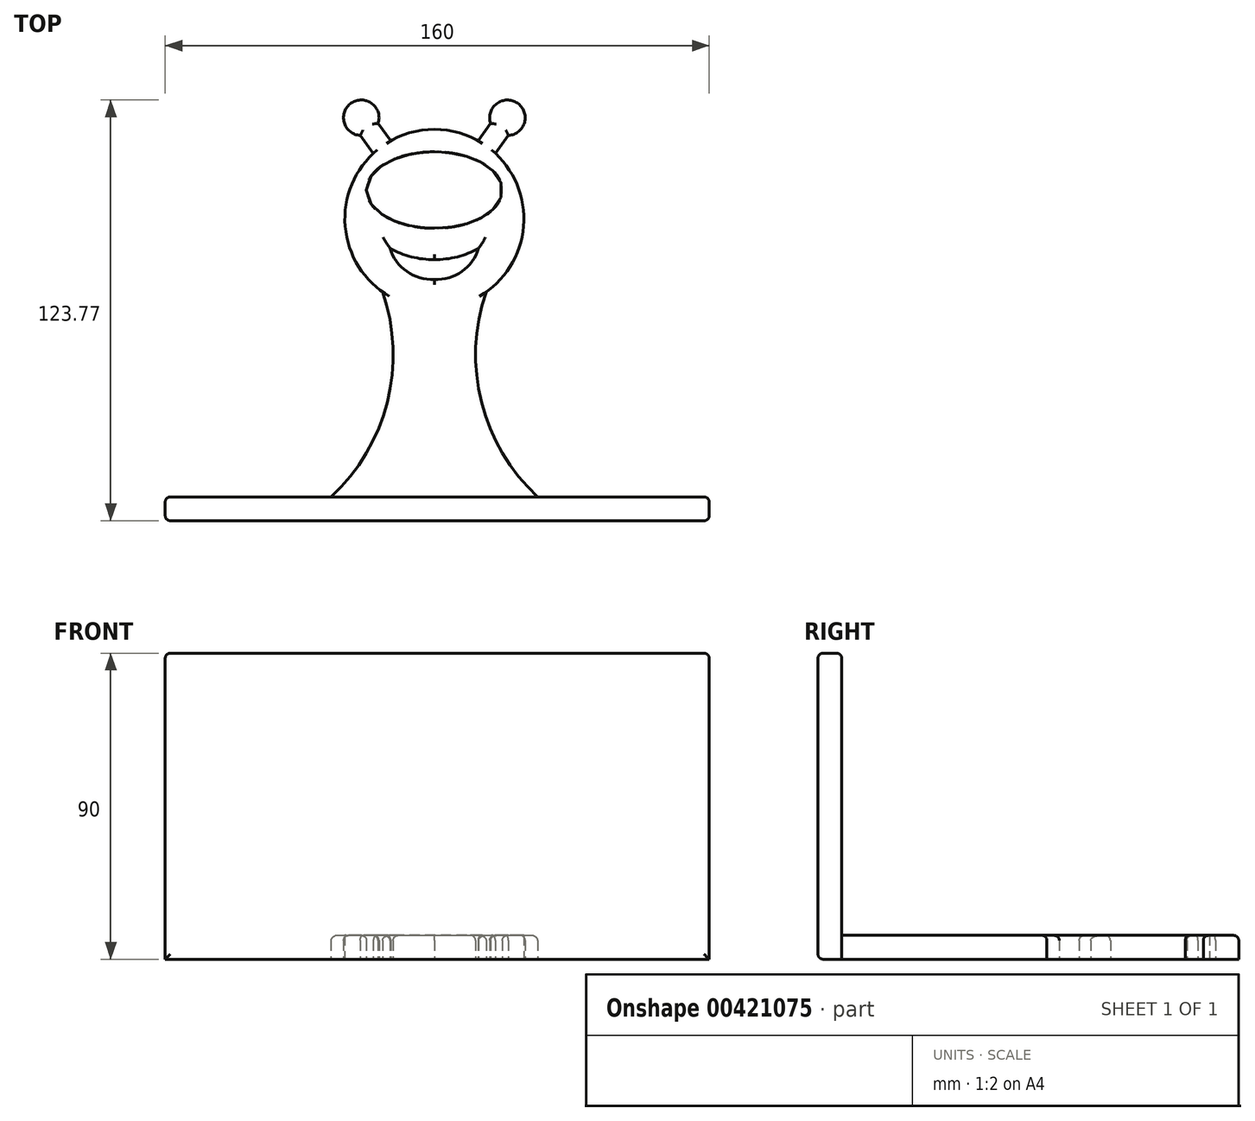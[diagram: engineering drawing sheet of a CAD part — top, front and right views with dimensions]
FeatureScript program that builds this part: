
annotation { "Feature Type Name" : "Feature", "Feature Type Description" : "" }
export const myFeature = defineFeature(function(context is Context, id is Id, definition is map)
    precondition{}
    {
        {
            var Q0;
            Q0=qCreatedBy(makeId("Top.planeOp"),FACE);
            var sketch = newSketch(context, id + "F0", { "sketchPlane" : qUnion([Q0])});
            skLineSegment(sketch, "E0", {"start": v(0, 25.53) * mm, "end": v(-30.48, 25.53) * mm});
            skArc(sketch, "E1", {"start": v(0, 25.53) * mm, "mid": v(-15.24, 73.33) * mm, "end": v(-30.48, 25.53) * mm});
            skArc(sketch, "E2", {"start": v(-45.92, -35.04) * mm, "mid": v(-29.13, -7.07) * mm, "end": v(-30.48, 25.53) * mm});
            skLineSegment(sketch, "E3", {"start": v(-45.92, -35.04) * mm, "end": v(-15.24, -35.04) * mm});
            skLineSegment(sketch, "E4", {"start": v(-15.24, 85.1) * mm, "end": v(-15.24, -44.22) * mm, "construction": true});
            skLineSegment(sketch, "E5.MirrorCS", {"start": v(-30.48, 25.53) * mm, "end": v(0, 25.53) * mm});
            skArc(sketch, "E6.MirrorCS", {"start": v(-30.48, 25.53) * mm, "mid": v(-15.24, 73.33) * mm, "end": v(0, 25.53) * mm});
            skArc(sketch, "E7.MirrorCS", {"start": v(15.44, -35.04) * mm, "mid": v(-1.35, -7.07) * mm, "end": v(0, 25.53) * mm});
            skLineSegment(sketch, "E8.MirrorCS", {"start": v(15.44, -35.04) * mm, "end": v(-15.24, -35.04) * mm});
            skLineSegment(sketch, "E9", {"start": v(-33.18, 66.27) * mm, "end": v(-37.04, 71.54) * mm});
            skLineSegment(sketch, "E10", {"start": v(-28.05, 70) * mm, "end": v(-31.78, 75.1) * mm});
            skArc(sketch, "E11", {"start": v(-31.78, 75.1) * mm, "mid": v(-39.66, 81.08) * mm, "end": v(-37.04, 71.54) * mm});
            skLineSegment(sketch, "E12.MirrorCS", {"start": v(-2.43, 70) * mm, "end": v(1.3, 75.1) * mm});
            skArc(sketch, "E13.MirrorCS", {"start": v(1.3, 75.1) * mm, "mid": v(9.18, 81.08) * mm, "end": v(6.56, 71.54) * mm});
            skLineSegment(sketch, "E14.MirrorCS", {"start": v(2.7, 66.27) * mm, "end": v(6.56, 71.54) * mm});
            skEllipse(sketch, "E15", {"center": v(-15.24, 55.48) * mm, "majorRadius": 20 * mm, "minorRadius": 11.25 * mm, "majorAxis": v(-1, 0)});
            skLineSegment(sketch, "E16", {"start": v(-50.04, 38.4) * mm, "end": v(18.05, 38.4) * mm, "construction": true});
            skArc(sketch, "E17", {"start": v(-28.27, 38.4) * mm, "mid": v(-23.35, 31.54) * mm, "end": v(-15.24, 29.2) * mm});
            skArc(sketch, "E18.MirrorCS", {"start": v(-2.21, 38.4) * mm, "mid": v(-7.13, 31.54) * mm, "end": v(-15.24, 29.2) * mm});
            skPoint(sketch, "E19", {"position": v(-51.66, 25.2) * mm});
            skArc(sketch, "E20", {"start": v(-28.27, 38.4) * mm, "mid": v(-21.98, 35.83) * mm, "end": v(-15.24, 35.05) * mm});
            skArc(sketch, "E21.MirrorCS", {"start": v(-2.21, 38.4) * mm, "mid": v(-8.5, 35.83) * mm, "end": v(-15.24, 35.05) * mm});
            skSolve(sketch);
        }
        {
            var Q0;
            Q0 = qSketchRegion(id + "F0", true);
            extrude(context, id + "F1", {"entities" : qUnion([Q0]), "depth" : 7 * mm, "offsetDistance" : 25 * mm});
        }
        {
            var Q0;
            Q0=makeQuery(id+"F1.opExtrude","SWEPT_FACE",FACE,{"disambiguationData":[OSD([sQuery(id+"F0.wireOp",EDGE,"E3"),sQuery(id+"F0.wireOp",EDGE,"E8.MirrorCS")])]});
            cPlane(context, id + "F2", {"entities" : qUnion([Q0]), "cplaneType" : CPlaneType.OFFSET, "offset" : 0.24 * mm, "oppositeDirection" : true, "width" : 150 * mm, "height" : 150 * mm});
        }
        {
            var Q0;
            Q0=qCreatedBy(id+"F2.planeOp",FACE);
            var sketch = newSketch(context, id + "F3", { "sketchPlane" : qUnion([Q0])});
            skLineSegment(sketch, "E22", {"start": v(-14.4, 9.68) * mm, "end": v(-14.4, -13.08) * mm, "construction": true});
            skLineSegment(sketch, "E23", {"start": v(-14.4, 0) * mm, "end": v(-94.4, 0) * mm});
            skLineSegment(sketch, "E24.MirrorCS", {"start": v(-14.4, 0) * mm, "end": v(65.6, 0) * mm});
            skLineSegment(sketch, "E25", {"start": v(-94.4, 0) * mm, "end": v(-94.4, 90) * mm});
            skLineSegment(sketch, "E26.MirrorCS", {"start": v(65.6, 0) * mm, "end": v(65.6, 90) * mm});
            skLineSegment(sketch, "E27", {"start": v(-94.4, 90) * mm, "end": v(65.6, 90) * mm});
            skSolve(sketch);
        }
        {
            var Q0;
            Q0 = qSketchRegion(id + "F3", true);
            extrude(context, id + "F4", {"entities" : qUnion([Q0]), "operationType" : NewBodyOperationType.ADD, "depth" : 7 * mm, "offsetDistance" : 25 * mm});
        }
        {
            var Q0;
            Q0=makeQuery(id+"F1.opExtrude","CAP_EDGE",EDGE,{"disambiguationData":[OSD([sQuery(id+"F0.wireOp",EDGE,"E13.MirrorCS")])],"isStart":false});
            var Q1;
            Q1=makeQuery(id+"F1.opExtrude","CAP_EDGE",EDGE,{"disambiguationData":[OSD([sQuery(id+"F0.wireOp",EDGE,"E12.MirrorCS")])],"isStart":false});
            var Q2;
            Q2=makeQuery(id+"F1.opExtrude","CAP_EDGE",EDGE,{"disambiguationData":[OSD([sQuery(id+"F0.wireOp",EDGE,"E14.MirrorCS")])],"isStart":false});
            var Q3;
            Q3=makeQuery(id+"F1.opExtrude","CAP_EDGE",EDGE,{"disambiguationData":[OSD([sQuery(id+"F0.wireOp",EDGE,"E11")])],"isStart":false});
            var Q4;
            Q4=makeQuery(id+"F1.opExtrude","CAP_EDGE",EDGE,{"disambiguationData":[OSD([sQuery(id+"F0.wireOp",EDGE,"E10")])],"isStart":false});
            var Q5;
            Q5=makeQuery(id+"F1.opExtrude","CAP_EDGE",EDGE,{"disambiguationData":[OSD([sQuery(id+"F0.wireOp",EDGE,"E9")])],"isStart":false});
            var Q6;
            {var subQ0=sQuery(id+"F0.wireOp",EDGE,"E6.MirrorCS");Q6=makeQuery(id+"F1.opExtrude","CAP_EDGE",EDGE,{"disambiguationData":[OSD([subQ0]),TDD([makeQuery(id+"F0.imprint","IMPRINT",EDGE,{"disambiguationData":[TD([[makeQuery(id+"F0.imprint","INTERSECT",VERTEX,{"derivedFrom":[subQ0,sQuery(id+"F0.wireOp",EDGE,"E10")]}),-1.0]])],"derivedFrom":subQ0})])],"isStart":false});}
            var Q7;
            {var subQ0=sQuery(id+"F0.wireOp",EDGE,"E6.MirrorCS");Q7=makeQuery(id+"F1.opExtrude","CAP_EDGE",EDGE,{"disambiguationData":[OSD([subQ0]),TDD([makeQuery(id+"F0.imprint","IMPRINT",EDGE,{"disambiguationData":[TD([[makeQuery(id+"F0.imprint","INTERSECT",VERTEX,{"derivedFrom":[subQ0,sQuery(id+"F0.wireOp",EDGE,"E9")]}),1.0]])],"derivedFrom":subQ0})])],"isStart":false});}
            var Q8;
            {var subQ0=sQuery(id+"F0.wireOp",EDGE,"E6.MirrorCS");Q8=makeQuery(id+"F1.opExtrude","CAP_EDGE",EDGE,{"disambiguationData":[OSD([subQ0]),TDD([makeQuery(id+"F0.imprint","IMPRINT",EDGE,{"disambiguationData":[TD([[makeQuery(id+"F0.imprint","INTERSECT",VERTEX,{"derivedFrom":[subQ0,sQuery(id+"F0.wireOp",EDGE,"E14.MirrorCS")]}),-1.0]])],"derivedFrom":subQ0})])],"isStart":false});}
            var Q9;
            Q9=makeQuery(id+"F1.opExtrude","CAP_EDGE",EDGE,{"disambiguationData":[OSD([sQuery(id+"F0.wireOp",EDGE,"E15")])],"isStart":false});
            var Q10;
            Q10=makeQuery(id+"F1.opExtrude","CAP_EDGE",EDGE,{"disambiguationData":[OSD([sQuery(id+"F0.wireOp",EDGE,"E20")])],"isStart":false});
            var Q11;
            Q11=makeQuery(id+"F1.opExtrude","CAP_EDGE",EDGE,{"disambiguationData":[OSD([sQuery(id+"F0.wireOp",EDGE,"E21.MirrorCS")])],"isStart":false});
            var Q12;
            Q12=makeQuery(id+"F1.opExtrude","CAP_EDGE",EDGE,{"disambiguationData":[OSD([sQuery(id+"F0.wireOp",EDGE,"E18.MirrorCS")])],"isStart":false});
            var Q13;
            Q13=makeQuery(id+"F1.opExtrude","CAP_EDGE",EDGE,{"disambiguationData":[OSD([sQuery(id+"F0.wireOp",EDGE,"E17")])],"isStart":false});
            var Q14;
            Q14=makeQuery(id+"F1.opExtrude","CAP_EDGE",EDGE,{"disambiguationData":[OSD([sQuery(id+"F0.wireOp",EDGE,"E7.MirrorCS")])],"isStart":false});
            var Q15;
            Q15=makeQuery(id+"F1.opExtrude","CAP_EDGE",EDGE,{"disambiguationData":[OSD([sQuery(id+"F0.wireOp",EDGE,"E2")])],"isStart":false});
            var Q16;
            Q16=makeQuery(id+"F4.opExtrude","CAP_EDGE",EDGE,{"disambiguationData":[OSD([sQuery(id+"F3.wireOp",EDGE,"E25")])],"isStart":true});
            var Q17;
            Q17=makeQuery(id+"F4.opExtrude","CAP_EDGE",EDGE,{"disambiguationData":[OSD([sQuery(id+"F3.wireOp",EDGE,"E27")])],"isStart":true});
            var Q18;
            Q18=makeQuery(id+"F4.opExtrude","CAP_EDGE",EDGE,{"disambiguationData":[OSD([sQuery(id+"F3.wireOp",EDGE,"E26.MirrorCS")])],"isStart":false});
            var Q19;
            Q19=makeQuery(id+"F4.opExtrude","CAP_FACE",FACE,{"disambiguationData":[OSD([sQuery(id+"F3.wireOp",EDGE,"E23"),sQuery(id+"F3.wireOp",EDGE,"E24.MirrorCS"),sQuery(id+"F3.wireOp",EDGE,"E25"),sQuery(id+"F3.wireOp",EDGE,"E26.MirrorCS"),sQuery(id+"F3.wireOp",EDGE,"E27")])],"isStart":false});
            var Q20;
            Q20=makeQuery(id+"F4.opExtrude","CAP_EDGE",EDGE,{"disambiguationData":[OSD([sQuery(id+"F3.wireOp",EDGE,"E23"),sQuery(id+"F3.wireOp",EDGE,"E24.MirrorCS")])],"isStart":false});
            var Q21;
            Q21=makeQuery(id+"F4.opExtrude","SWEPT_FACE",FACE,{"disambiguationData":[OSD([sQuery(id+"F3.wireOp",EDGE,"E27")])]});
            var Q22;
            Q22=makeQuery(id+"F4.opExtrude","CAP_EDGE",EDGE,{"disambiguationData":[OSD([sQuery(id+"F3.wireOp",EDGE,"E26.MirrorCS")])],"isStart":true});
            fillet(context, id + "F5", {"entities" : qUnion([Q0, Q1, Q2, Q3, Q4, Q5, Q6, Q7, Q8, Q9, Q10, Q11, Q12, Q13, Q14, Q15, Q16, Q17, Q18, Q19, Q20, Q21, Q22]), "radius" : 1.5 * mm, "tangentPropagation" : true, "allowEdgeOverflow" : false});
        }
    });
